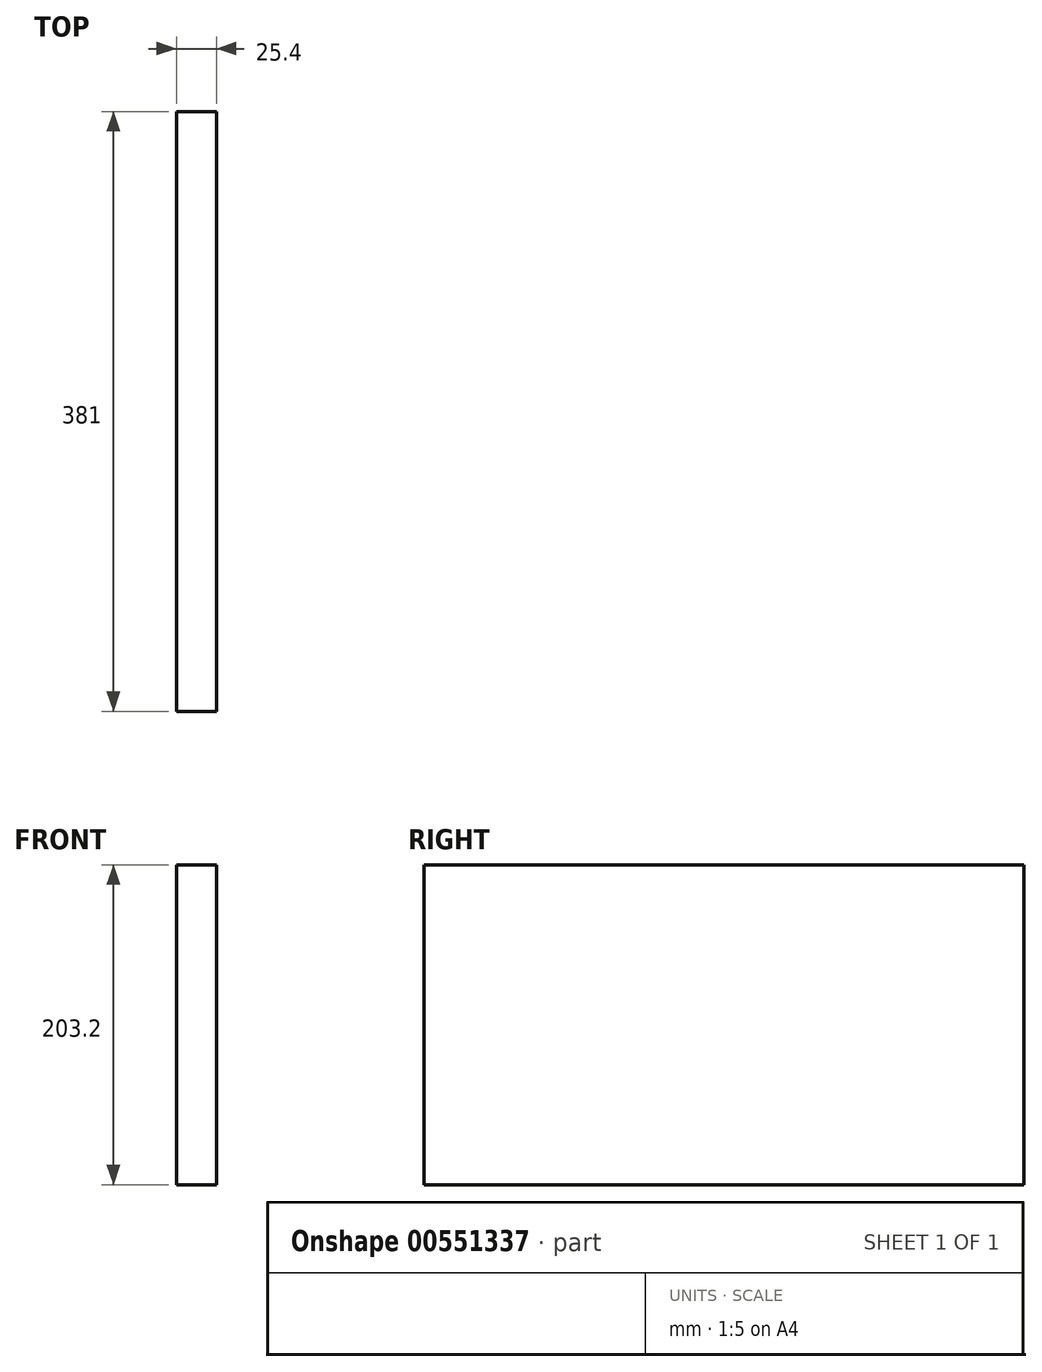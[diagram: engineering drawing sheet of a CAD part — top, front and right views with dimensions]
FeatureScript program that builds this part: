
annotation { "Feature Type Name" : "Feature", "Feature Type Description" : "" }
export const myFeature = defineFeature(function(context is Context, id is Id, definition is map)
    precondition{}
    {
        {
            var Q0;
            Q0=qCreatedBy(makeId("Right.planeOp"),FACE);
            var sketch = newSketch(context, id + "F0", { "sketchPlane" : qUnion([Q0])});
            skLineSegment(sketch, "E0.bottom", {"start": v(265.59, 108.16) * mm, "end": v(-115.41, 108.16) * mm});
            skLineSegment(sketch, "E0.top", {"start": v(265.59, -95.04) * mm, "end": v(-115.41, -95.04) * mm});
            skLineSegment(sketch, "E0.left", {"start": v(265.59, 108.16) * mm, "end": v(265.59, -95.04) * mm});
            skLineSegment(sketch, "E0.right", {"start": v(-115.41, 108.16) * mm, "end": v(-115.41, -95.04) * mm});
            skSolve(sketch);
        }
        {
            var Q0;
            Q0 = qSketchRegion(id + "F0", true);
            extrude(context, id + "F1", {"entities" : qUnion([Q0]), "depth" : 25.4 * mm, "offsetDistance" : 25.4 * mm});
        }
    });
